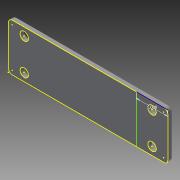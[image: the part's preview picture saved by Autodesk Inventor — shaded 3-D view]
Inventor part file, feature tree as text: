
AUTODESK INVENTOR PART (.ipt)
format: ipt  version: 2013 (Build 170138000, 138)  size: 107,008 bytes
history: native  units: in
note: dims shown in document units (in); Inventor stores cm internally (conversion verified against a paired STEP export)
features: sketch x3, extrude x2, fillet x1
ambient origin geometry x8: Origin, YZ Plane, XZ Plane, XY Plane, X Axis, Y Axis, Z Axis, Center Point
bodies: Solid1 (feature_tree)
feature tree (6):
  extrude  "Extrusion1"  Depth=5.046in
  extrude  "Extrusion2"  Depth=0.5in
  fillet  "Fillet1"  Radius=0.25in
  sketch  "Sketch3"  dims[d6=1.0in d7=0.266in d8=0.266in d9=0.5in d10=0.25in d11=0.266in d12=0.266in d13=1.0in d14=0.125in d15=0.0in d16=0.125in d17=1.0in]
  sketch  "Sketch1"  dims[d0=1.5in d1=5.046in]
  sketch  "Sketch2"  dims[d2=0.125in d3=0.0in d4=0.5in d5=0.25in]
